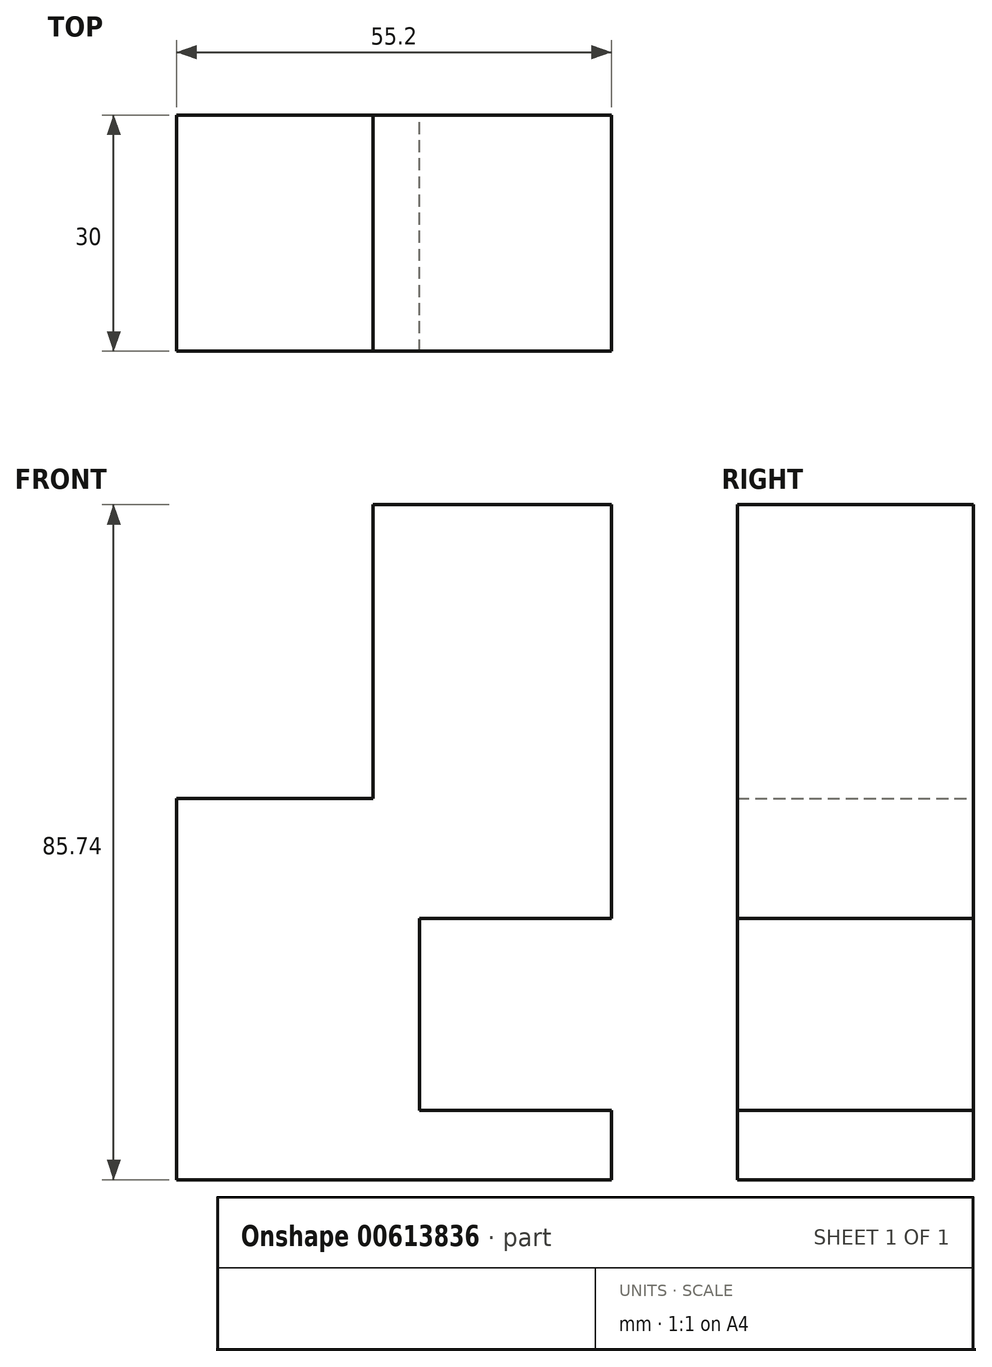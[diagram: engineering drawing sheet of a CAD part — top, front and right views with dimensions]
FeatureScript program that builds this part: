
annotation { "Feature Type Name" : "Feature", "Feature Type Description" : "" }
export const myFeature = defineFeature(function(context is Context, id is Id, definition is map)
    precondition{}
    {
        {
            var Q0;
            Q0=qCreatedBy(makeId("Front.planeOp"),FACE);
            var sketch = newSketch(context, id + "F0", { "sketchPlane" : qUnion([Q0])});
            skLineSegment(sketch, "E0.bottom", {"start": v(-59.75, 45.22) * mm, "end": v(-29.5, 45.22) * mm});
            skLineSegment(sketch, "E0.top", {"start": v(-53.88, -7.34) * mm, "end": v(-29.5, -7.34) * mm});
            skLineSegment(sketch, "E0.left", {"start": v(-59.75, 45.22) * mm, "end": v(-59.75, 7.93) * mm});
            skLineSegment(sketch, "E0.right", {"start": v(-29.5, 45.22) * mm, "end": v(-29.5, -7.34) * mm});
            skLineSegment(sketch, "E1.bottom", {"start": v(-84.7, 7.93) * mm, "end": v(-59.75, 7.93) * mm});
            skLineSegment(sketch, "E1.top", {"start": v(-84.7, -40.52) * mm, "end": v(-53.88, -40.52) * mm});
            skLineSegment(sketch, "E1.left", {"start": v(-84.7, 7.93) * mm, "end": v(-84.7, -40.52) * mm});
            skLineSegment(sketch, "E1.right", {"start": v(-53.88, -7.34) * mm, "end": v(-53.88, -31.71) * mm});
            skLineSegment(sketch, "E2.bottom", {"start": v(-53.88, -40.52) * mm, "end": v(-29.5, -40.52) * mm});
            skLineSegment(sketch, "E2.top", {"start": v(-53.88, -31.71) * mm, "end": v(-29.5, -31.71) * mm});
            skLineSegment(sketch, "E2.right", {"start": v(-29.5, -40.52) * mm, "end": v(-29.5, -31.71) * mm});
            skSolve(sketch);
        }
        {
            var Q0;
            Q0 = qSketchRegion(id + "F0", true);
            extrude(context, id + "F1", {"entities" : qUnion([Q0]), "depth" : 30 * mm, "offsetDistance" : 25 * mm});
        }
    });
